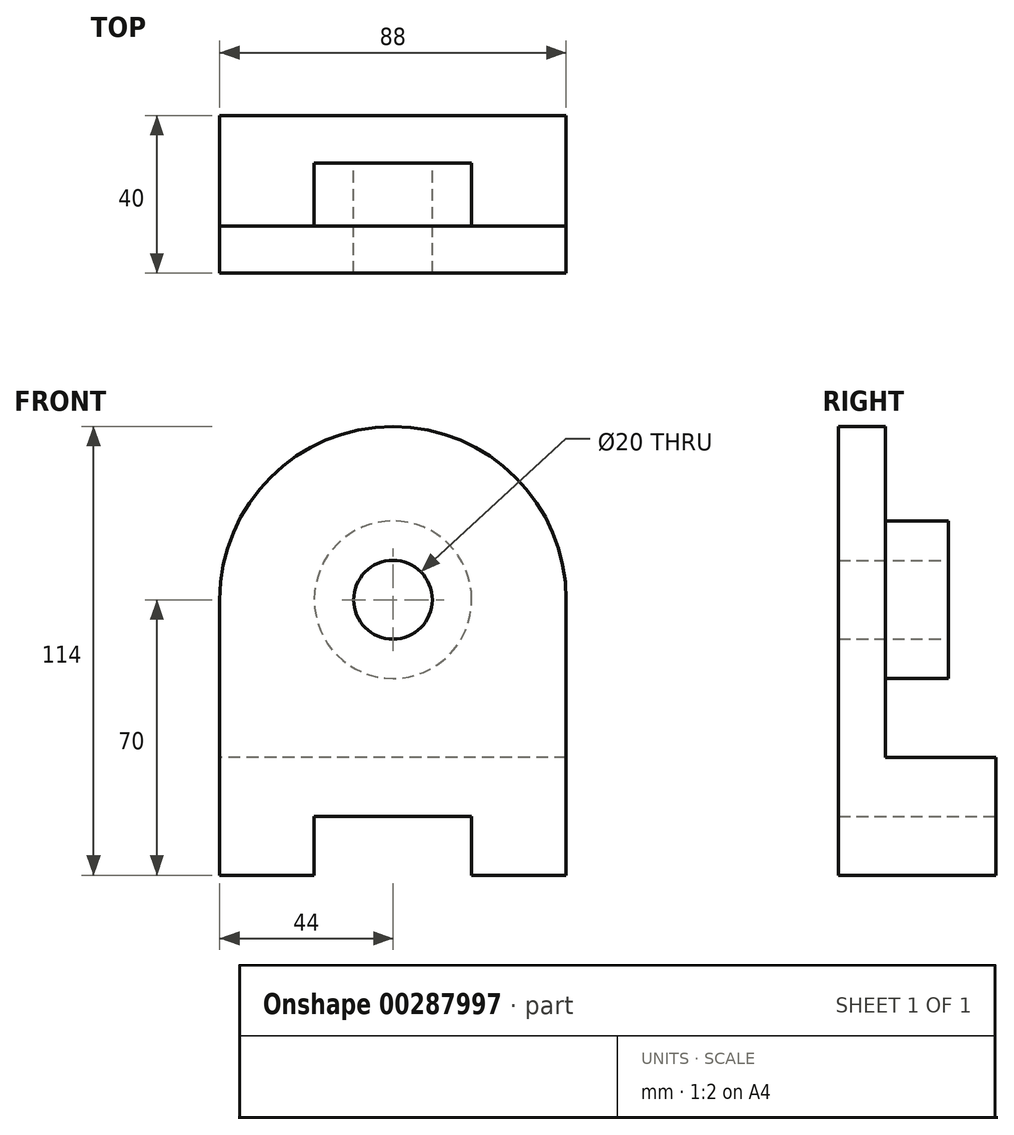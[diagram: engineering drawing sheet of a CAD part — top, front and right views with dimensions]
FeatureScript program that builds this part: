
annotation { "Feature Type Name" : "Feature", "Feature Type Description" : "" }
export const myFeature = defineFeature(function(context is Context, id is Id, definition is map)
    precondition{}
    {
        {
            var Q0;
            Q0=qCreatedBy(makeId("Front.planeOp"),FACE);
            var sketch = newSketch(context, id + "F0", { "sketchPlane" : qUnion([Q0])});
            skLineSegment(sketch, "E0", {"start": v(-44, -40) * mm, "end": v(-44, 0) * mm});
            skLineSegment(sketch, "E1", {"start": v(0, 44) * mm, "end": v(0, 44) * mm});
            skLineSegment(sketch, "E2", {"start": v(44, 0) * mm, "end": v(44, -40) * mm});
            skLineSegment(sketch, "E3", {"start": v(44, -40) * mm, "end": v(-44, -40) * mm});
            skLineSegment(sketch, "E4", {"start": v(-44, -70) * mm, "end": v(-20, -70) * mm});
            skLineSegment(sketch, "E5", {"start": v(-20, -70) * mm, "end": v(-20, -55) * mm});
            skLineSegment(sketch, "E6", {"start": v(-20, -55) * mm, "end": v(20, -55) * mm});
            skLineSegment(sketch, "E7", {"start": v(20, -55) * mm, "end": v(20, -70) * mm});
            skLineSegment(sketch, "E8", {"start": v(20, -70) * mm, "end": v(44, -70) * mm});
            skLineSegment(sketch, "E9", {"start": v(44, -70) * mm, "end": v(44, -40) * mm});
            skLineSegment(sketch, "E10", {"start": v(-44, -40) * mm, "end": v(-44, -70) * mm});
            skCircle(sketch, "E11", {"center": v(0, 0) * mm, "radius": 20 * mm});
            skCircle(sketch, "E12", {"center": v(0, 0) * mm, "radius": 10 * mm});
            skPoint(sketch, "E13.visualSharp", {"position": v(-44, 44) * mm});
            skArc(sketch, "E13.filletArc", {"start": v(0, 44) * mm, "mid": v(-31.11, 31.11) * mm, "end": v(-44, 0) * mm});
            skPoint(sketch, "E14.visualSharp", {"position": v(44, 44) * mm});
            skArc(sketch, "E14.filletArc", {"start": v(44, 0) * mm, "mid": v(31.11, 31.11) * mm, "end": v(0, 44) * mm});
            skSolve(sketch);
        }
        {
            var Q0;
            Q0=makeQuery(id+"F0.imprint","IMPRINT",FACE,{"disambiguationData":[TD([[makeQuery(id+"F0.imprint","IMPRINT",EDGE,{"derivedFrom":sQuery(id+"F0.wireOp",EDGE,"E3")}),1.0]])]});
            extrude(context, id + "F1", {"entities" : qUnion([Q0]), "depth" : 12 * mm, "hasSecondDirection" : true, "secondDirectionOppositeDirection" : true, "secondDirectionDepth" : 28 * mm});
        }
        {
            var Q0;
            Q0 = qSketchRegion(id + "F0", true);
            extrude(context, id + "F2", {"entities" : qUnion([Q0]), "operationType" : NewBodyOperationType.ADD, "depth" : 12 * mm});
        }
        {
            var Q0;
            Q0=makeQuery(id+"F0.imprint","IMPRINT",FACE,{"disambiguationData":[TD([[makeQuery(id+"F0.imprint","IMPRINT",EDGE,{"derivedFrom":sQuery(id+"F0.wireOp",EDGE,"E11")}),1.0]])]});
            extrude(context, id + "F3", {"entities" : qUnion([Q0]), "operationType" : NewBodyOperationType.ADD, "depth" : 12 * mm, "hasSecondDirection" : true, "secondDirectionOppositeDirection" : true, "secondDirectionDepth" : 16 * mm});
        }
    });
